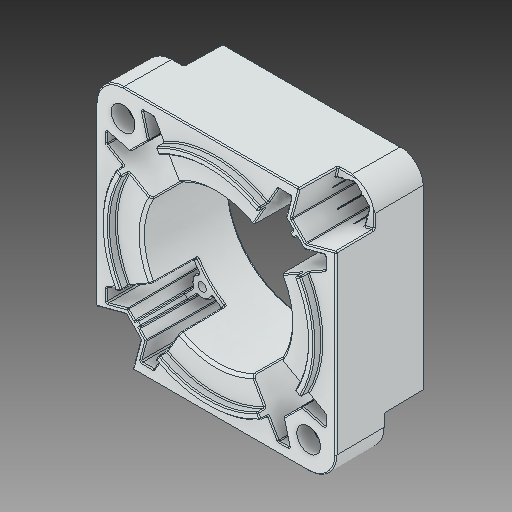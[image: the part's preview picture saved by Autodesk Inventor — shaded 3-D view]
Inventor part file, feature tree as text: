
AUTODESK INVENTOR PART (.ipt)
format: ipt  version: 2019 (Build 230136000, 136)  size: 1,595,904 bytes
history: native  units: in
note: dims shown in document units (in); Inventor stores cm internally (conversion verified against a paired STEP export)
features: chamfer x1
ambient origin geometry x8: Origin, YZ Plane, XZ Plane, XY Plane, X Axis, Y Axis, Z Axis, Center Point
bodies: Solid1 (feature_tree)
feature tree (1):
  chamfer  "Chamfer2"  [1 undecoded]
note: 1 required parameter value undecoded (feature->parameter linkage not recoverable at this tier; creation-order binding heuristic only, values carry confidence <= 0.55)
